# Revit family: SL1
name_source: partatom
category: Lighting Fixtures
revit_build: Autodesk Revit 2014 (Build: 20130308_1515(x64)
units: mm (PartAtom-declared; Revit-internal decimal feet)

## types (1)
- SL1
    Apparent Load = 56 VA
    Assembly Code = D5020200
    Color Filter = 16777215
    Description = Sight Lightforms are specifically designed and engineered to combine contemporary form with rugged vandal-resistant construction. All fixture heads are heavy-wall one-piece aluminum castings and head to shaft connections are concealed for greater strength and clean detailing.
    Diameter = 5 "
    Dimming Lamp Color Temperature Shift = <None>
    Emit Shape Visible in Rendering = No
    Emit from Rectangle Length = 4 "
    Emit from Rectangle Width = 4 "
    Finish = Powder Coat-Kim-White
    Glass = Glass-KIM-Temper Molded
    Height = 24 "
    Lamp = LED
    Load Classification = Lighting
    Manufacturer = Kim Lighting
    MasterFormat Title = Landscape Lighting, Site Lighting, Walkway Lighting
    Model = Site Lightforms
    Number of Poles = 1
    Photometric Notes = More IES files download on Photometric Web Link
    Photometric Web File = sl1-36l3k.ies
    Photometric Web Link = https://www.hubbell.com
    Power Factor = 1
    Product Documentation Link = https://hubbellcdn.com
    Product Page URL = https://www.hubbell.com
    Radius = 2.5 "
    Series = Site Lightforms
    Tilt Angle = 60.00°
    Type Comments = Light Fixture
    URL = https://www.hubbell.com
    Voltage = 120 V
    Wattage Comments = default

## geometry (parser evidence)
native form markers: Sweep x2
no freeform markers — native parametric forms only
